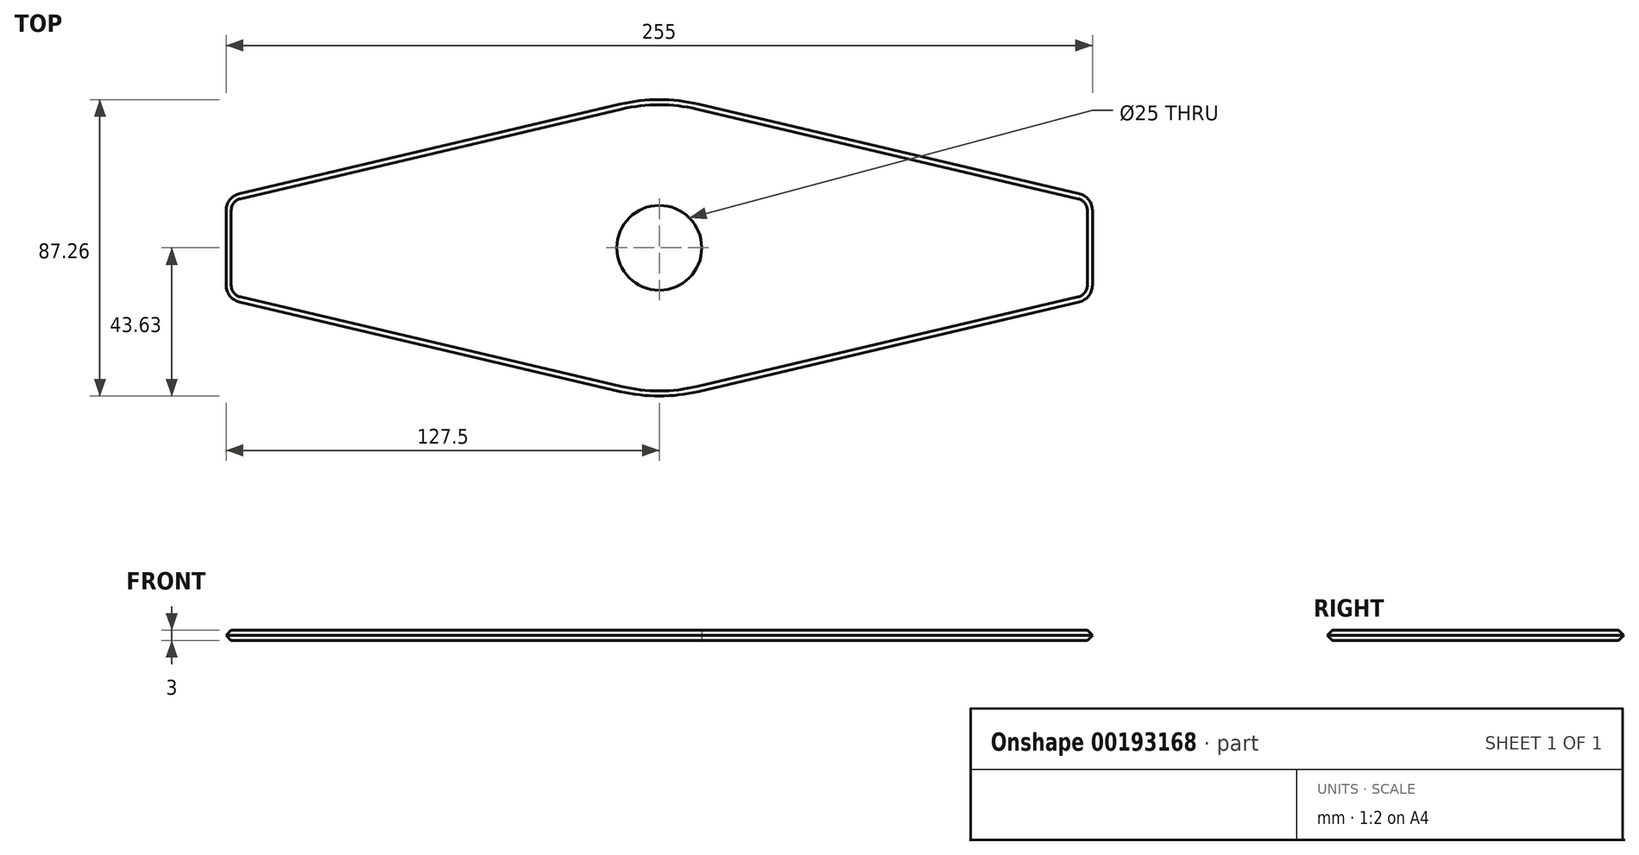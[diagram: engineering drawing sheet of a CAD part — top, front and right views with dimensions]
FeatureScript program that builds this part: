
annotation { "Feature Type Name" : "Feature", "Feature Type Description" : "" }
export const myFeature = defineFeature(function(context is Context, id is Id, definition is map)
    precondition{}
    {
        {
            var Q0;
            Q0=qCreatedBy(makeId("Top.planeOp"),FACE);
            var sketch = newSketch(context, id + "F0", { "sketchPlane" : qUnion([Q0])});
            skCircle(sketch, "E0", {"center": v(0, 0) * mm, "radius": 12.5 * mm});
            skLineSegment(sketch, "E1.bottom", {"start": v(-127.5, 45) * mm, "end": v(127.5, 45) * mm, "construction": true});
            skLineSegment(sketch, "E1.top", {"start": v(-127.5, -45) * mm, "end": v(127.5, -45) * mm, "construction": true});
            skLineSegment(sketch, "E1.left", {"start": v(-127.5, 45) * mm, "end": v(-127.5, -45) * mm, "construction": true});
            skLineSegment(sketch, "E1.right", {"start": v(127.5, 45) * mm, "end": v(127.5, -45) * mm, "construction": true});
            skLineSegment(sketch, "E2.bottom", {"start": v(-127.5, 15) * mm, "end": v(127.5, 15) * mm, "construction": true});
            skLineSegment(sketch, "E2.top", {"start": v(-127.5, -15) * mm, "end": v(127.5, -15) * mm, "construction": true});
            skLineSegment(sketch, "E2.left", {"start": v(-127.5, 15) * mm, "end": v(-127.5, -15) * mm, "construction": true});
            skLineSegment(sketch, "E2.right", {"start": v(127.5, 15) * mm, "end": v(127.5, -15) * mm, "construction": true});
            skLineSegment(sketch, "E3", {"start": v(0, 45) * mm, "end": v(0, -45) * mm, "construction": true});
            skLineSegment(sketch, "E4", {"start": v(0, 45) * mm, "end": v(127.5, 15) * mm});
            skLineSegment(sketch, "E5", {"start": v(127.5, -15) * mm, "end": v(0, -45) * mm});
            skLineSegment(sketch, "E6", {"start": v(0, -45) * mm, "end": v(-127.5, -15) * mm});
            skLineSegment(sketch, "E7", {"start": v(-127.5, 15) * mm, "end": v(0, 45) * mm});
            skLineSegment(sketch, "E8", {"start": v(-127.5, 15) * mm, "end": v(-127.5, -15) * mm});
            skLineSegment(sketch, "E9", {"start": v(127.5, -15) * mm, "end": v(127.5, 15) * mm});
            skLineSegment(sketch, "E10.0", {"start": v(-50, 45) * mm, "end": v(-50, -45) * mm, "construction": true});
            skLineSegment(sketch, "E11.0", {"start": v(50, 45) * mm, "end": v(50, -45) * mm, "construction": true});
            skPoint(sketch, "E12", {"position": v(-50, 33.24) * mm});
            skPoint(sketch, "E13", {"position": v(50, 33.24) * mm});
            skPoint(sketch, "E14", {"position": v(50, -33.24) * mm});
            skPoint(sketch, "E15", {"position": v(-50, -33.24) * mm});
            skSolve(sketch);
        }
        {
            var Q0;
            Q0=makeQuery(id+"F0.imprint","IMPRINT",FACE,{"disambiguationData":[TD([[makeQuery(id+"F0.imprint","IMPRINT",EDGE,{"derivedFrom":sQuery(id+"F0.wireOp",EDGE,"E0")}),-1.0]])]});
            extrude(context, id + "F1", {"entities" : qUnion([Q0]), "depth" : 3 * mm});
        }
        {
            var Q0;
            Q0=makeQuery(id+"F1.opExtrude","SWEPT_EDGE",EDGE,{"disambiguationData":[OSD([sQuery(id+"F0.wireOp",EDGE,"E4"),sQuery(id+"F0.wireOp",EDGE,"E7")])]});
            var Q1;
            Q1=makeQuery(id+"F1.opExtrude","SWEPT_EDGE",EDGE,{"disambiguationData":[OSD([sQuery(id+"F0.wireOp",EDGE,"E5"),sQuery(id+"F0.wireOp",EDGE,"E6")])]});
            fillet(context, id + "F2", {"entities" : qUnion([Q0, Q1]), "radius" : 50 * mm, "tangentPropagation" : true, "allowEdgeOverflow" : false});
        }
        {
            var Q0;
            Q0=makeQuery(id+"F1.opExtrude","SWEPT_EDGE",EDGE,{"disambiguationData":[OSD([sQuery(id+"F0.wireOp",EDGE,"E4"),sQuery(id+"F0.wireOp",EDGE,"E9")])]});
            var Q1;
            Q1=makeQuery(id+"F1.opExtrude","SWEPT_EDGE",EDGE,{"disambiguationData":[OSD([sQuery(id+"F0.wireOp",EDGE,"E5"),sQuery(id+"F0.wireOp",EDGE,"E9")])]});
            var Q2;
            Q2=makeQuery(id+"F1.opExtrude","SWEPT_EDGE",EDGE,{"disambiguationData":[OSD([sQuery(id+"F0.wireOp",EDGE,"E7"),sQuery(id+"F0.wireOp",EDGE,"E8")])]});
            var Q3;
            Q3=makeQuery(id+"F1.opExtrude","SWEPT_EDGE",EDGE,{"disambiguationData":[OSD([sQuery(id+"F0.wireOp",EDGE,"E6"),sQuery(id+"F0.wireOp",EDGE,"E8")])]});
            fillet(context, id + "F3", {"entities" : qUnion([Q0, Q1, Q2, Q3]), "radius" : 5 * mm, "tangentPropagation" : true, "allowEdgeOverflow" : false});
        }
        {
            var Q0;
            Q0=makeQuery(id+"F1.opExtrude","CAP_EDGE",EDGE,{"disambiguationData":[OSD([sQuery(id+"F0.wireOp",EDGE,"E7")])],"isStart":false});
            var Q1;
            Q1=makeQuery(id+"F1.opExtrude","CAP_EDGE",EDGE,{"disambiguationData":[OSD([sQuery(id+"F0.wireOp",EDGE,"E7")])],"isStart":true});
            chamfer(context, id + "F4", {"entities" : qUnion([Q0, Q1]), "width" : 1.5 * mm, "tangentPropagation" : true});
        }
    });
